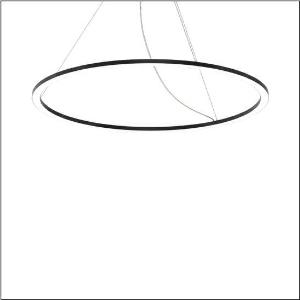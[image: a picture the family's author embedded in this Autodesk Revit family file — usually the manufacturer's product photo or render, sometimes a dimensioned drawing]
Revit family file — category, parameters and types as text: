
# Revit family: silica_r__21_ring-d_5pjbd4d3104a_b1c8
name_source: partatom
category: Lighting Fixtures
units: mm (PartAtom-declared; Revit-internal decimal feet)

## family parameters
Cut with Voids When Loaded = No
Host = Face
Light Source = No
Part Type = Normal
Room Calculation Point = No
Round Connector Dimension = Use Diameter
Shared = No

## types (1)
- Silica® 21 Ring-D (1 x LED, 11350 lm, 125 W, 4000K)
    Apparent Load = 125 VA
    CIE Flux Codes = 37 69 92 100 100
    Color Rendering = 80
    Color Temperature = 4000K
    Default Elevation = 1800 mm
    Description = Silica® 21 Ring-D, suspended luminaire, of PMMA, frosted, light emission: ring underside luminous distribution, primary light characteristic: symmetric, installation type: suspended mounting, LED, rated luminous flux: 11.350lm, luminous efficacy: 91lm/W, light colour: 840, colour temperature: 4000K, with terminal, 5-pole, mains connection: 230V, AC/DC, 0/50..60Hz, rated input power: 125W, housing, of extruded aluminium section, jet black (RAL 9005), diameter: 1.450mm, ceiling canopy, jet black (RAL 9005), protection rating (lamp compartment): IP40, protection rating (control gear compartment): IP40, insulation class (complete): insulation class I (protective earthing), certification: CE, impact resistance: IK02, permissible operating ambient temperature: 0..+35°C, packaging unit: 1 piece
    Height = 25 mm  [stored 0.082021 ft]
    Lamp = 1 x LED
    Lamp Light Flux = 11350 lm
    Lamp Power = 125 W
    Lamp count = 1
    Length = 1450 mm
    Luminous efficacy = 91 lm/W
    Manufacturer = Siteco
    ModVariant = No
    Model = 5PJBD4D3104A
    Mounting Place = Ceiling
    Mounting Type = Pendant
    Number of Poles = 1
    OnlyDefault = Yes
    Power Factor = 1
    Product Name = Silica® 21 Ring-D
    Product group = suspended luminaire
    ProductGroupID = 904
    Protection Class = Protection class I
    Protection Degree = Degree of protection
    RLX_Detail_Level = 1
    RLX_Emergency_Light_Flux = 0 lm
    RLX_Emergency_Type = 0
    RLX_Emergency_Type_DB = No
    RlxData = <blob elided: 19409 chars, md5=227fb699>
    Socket = socket
    Standby Power = 0 W
    System Light Flux = 11350 lm
    System Power = 125 W
    Type Comments = Product without accessories
    Type Image = l_1258357.jpg
    URL = http://relux.com
    VarID = ---
    Voltage = 0 V
    Weight = 0.00 kg
    Width = 0 mm  [stored 0 ft]

note: [stored X ft] marks values corroborated as IEEE doubles in the binary element streams (Revit-internal decimal feet)

## geometry (parser evidence)
native form markers: Blend x4, Sweep x12
no freeform markers — native parametric forms only
